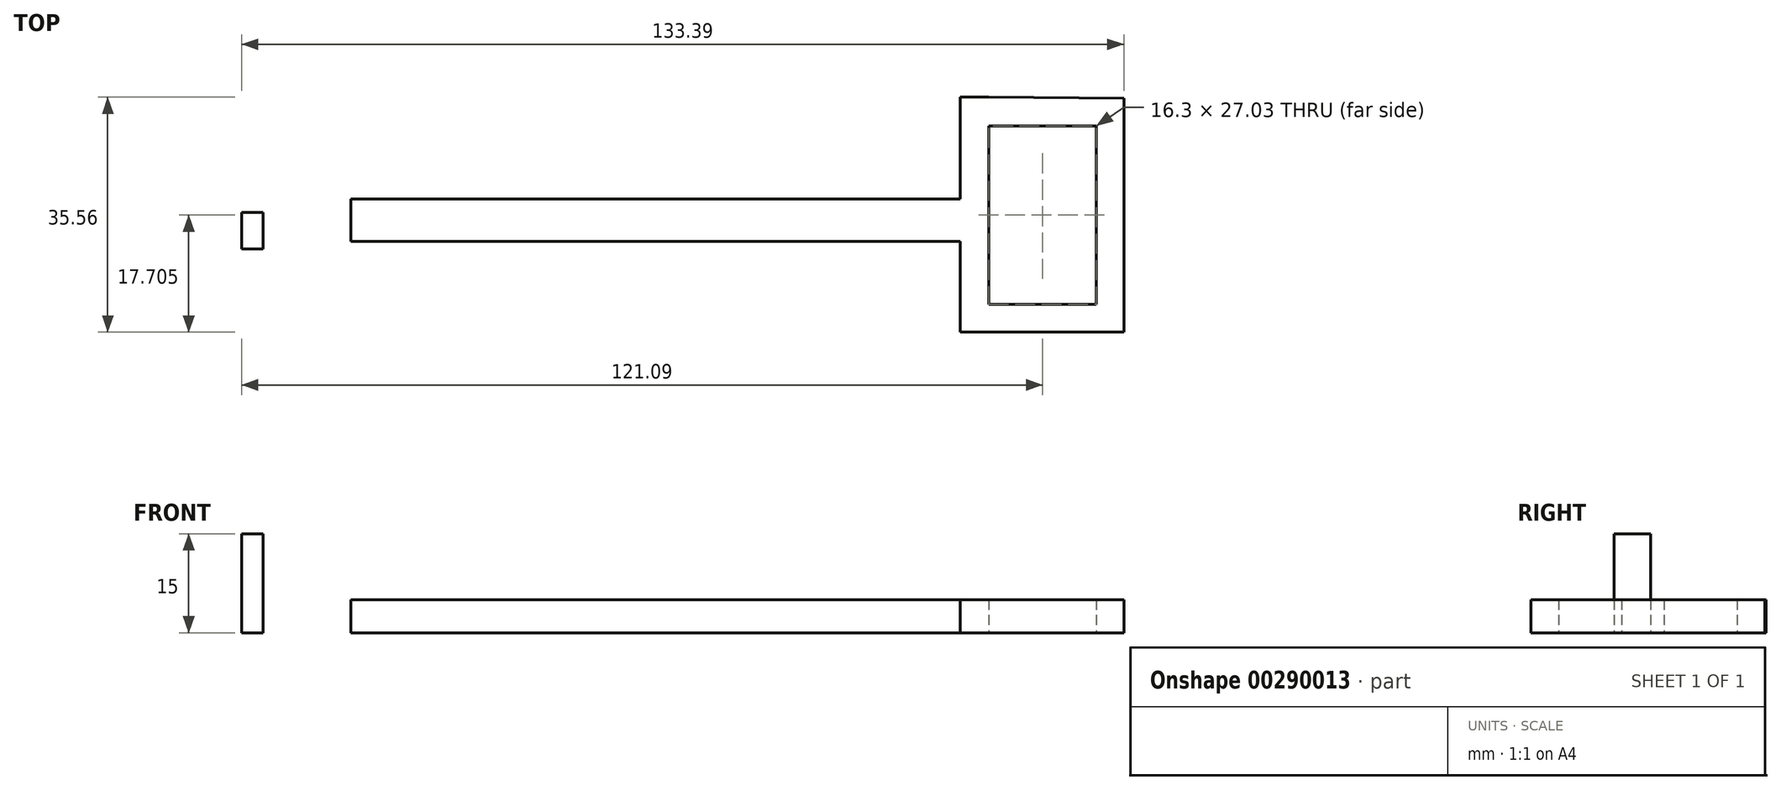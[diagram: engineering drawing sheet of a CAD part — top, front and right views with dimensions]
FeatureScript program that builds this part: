
annotation { "Feature Type Name" : "Feature", "Feature Type Description" : "" }
export const myFeature = defineFeature(function(context is Context, id is Id, definition is map)
    precondition{}
    {
        {
            var Q0;
            Q0=qCreatedBy(makeId("Top.planeOp"),FACE);
            var sketch = newSketch(context, id + "F0", { "sketchPlane" : qUnion([Q0])});
            skLineSegment(sketch, "E0.bottom", {"start": v(-7.6, -2.33) * mm, "end": v(42.14, -2.33) * mm});
            skLineSegment(sketch, "E0.top", {"start": v(-7.6, -8.73) * mm, "end": v(42.14, -8.73) * mm});
            skLineSegment(sketch, "E0.left", {"start": v(-7.6, -2.33) * mm, "end": v(-7.6, -8.73) * mm});
            skLineSegment(sketch, "E0.right", {"start": v(42.14, -2.33) * mm, "end": v(42.14, -8.73) * mm});
            skLineSegment(sketch, "E1.bottom", {"start": v(42.14, 13.07) * mm, "end": v(46.41, 13.07) * mm});
            skLineSegment(sketch, "E1.top", {"start": v(42.14, -22.49) * mm, "end": v(46.41, -22.49) * mm});
            skLineSegment(sketch, "E1.left", {"start": v(42.14, 13.07) * mm, "end": v(42.14, -22.49) * mm});
            skLineSegment(sketch, "E1.right", {"start": v(46.41, 13.07) * mm, "end": v(46.41, -22.49) * mm});
            skLineSegment(sketch, "E2.top", {"start": v(46.41, 8.73) * mm, "end": v(66.86, 8.73) * mm});
            skLineSegment(sketch, "E2.left", {"start": v(46.41, 13.07) * mm, "end": v(46.41, 8.73) * mm});
            skLineSegment(sketch, "E3.bottom", {"start": v(46.41, -22.49) * mm, "end": v(66.86, -22.49) * mm});
            skLineSegment(sketch, "E3.top", {"start": v(46.41, -18.3) * mm, "end": v(66.86, -18.3) * mm});
            skLineSegment(sketch, "E3.left", {"start": v(46.41, -22.49) * mm, "end": v(46.41, -18.3) * mm});
            skLineSegment(sketch, "E3.right", {"start": v(66.86, -22.49) * mm, "end": v(66.86, -18.3) * mm});
            skLineSegment(sketch, "E4.bottom", {"start": v(66.86, -18.3) * mm, "end": v(62.7, -18.3) * mm});
            skLineSegment(sketch, "E4.top", {"start": v(66.86, 8.73) * mm, "end": v(62.7, 8.73) * mm});
            skLineSegment(sketch, "E4.left", {"start": v(66.86, -18.3) * mm, "end": v(66.86, 8.73) * mm});
            skLineSegment(sketch, "E4.right", {"start": v(62.7, -18.3) * mm, "end": v(62.7, 8.73) * mm});
            skLineSegment(sketch, "E5", {"start": v(66.86, 12.91) * mm, "end": v(46.41, 13.07) * mm});
            skLineSegment(sketch, "E6", {"start": v(66.86, 12.91) * mm, "end": v(66.86, 8.73) * mm});
            skLineSegment(sketch, "E7", {"start": v(-7.6, -8.73) * mm, "end": v(-50.02, -8.73) * mm});
            skLineSegment(sketch, "E8", {"start": v(-50.02, -8.73) * mm, "end": v(-50.02, -2.33) * mm});
            skLineSegment(sketch, "E9", {"start": v(-50.02, -2.33) * mm, "end": v(-7.6, -2.33) * mm});
            skSolve(sketch);
        }
        {
            var Q0;
            Q0=makeQuery(id+"F0.imprint","IMPRINT",FACE,{"disambiguationData":[TD([[makeQuery(id+"F0.imprint","IMPRINT",EDGE,{"derivedFrom":sQuery(id+"F0.wireOp",EDGE,"E0.bottom")}),-1.0]])]});
            extrude(context, id + "F1", {"entities" : qUnion([Q0]), "depth" : 5 * mm});
        }
        {
            var Q0;
            Q0 = qSketchRegion(id + "F0", true);
            extrude(context, id + "F2", {"entities" : qUnion([Q0]), "operationType" : NewBodyOperationType.ADD, "depth" : 5 * mm});
        }
        {
            var Q0;
            Q0 = qSketchRegion(id + "F0", true);
            var sketch = newSketch(context, id + "F3", { "sketchPlane" : qUnion([Q0])});
            skLineSegment(sketch, "E10.KFZB.KFZB", {"start": v(-50.02, -2.33) * mm, "end": v(-7.6, -2.33) * mm, "construction": true});
            skArc(sketch, "E10.0.endCap", {"start": v(-7.6, 0.17) * mm, "mid": v(-5.1, -2.33) * mm, "end": v(-7.6, -4.83) * mm});
            skLineSegment(sketch, "E11.bottom", {"start": v(-66.53, -9.92) * mm, "end": v(-63.33, -9.92) * mm});
            skLineSegment(sketch, "E11.top", {"start": v(-66.53, -4.4) * mm, "end": v(-63.33, -4.4) * mm});
            skLineSegment(sketch, "E11.left", {"start": v(-66.53, -9.92) * mm, "end": v(-66.53, -4.4) * mm});
            skLineSegment(sketch, "E11.right", {"start": v(-63.33, -9.92) * mm, "end": v(-63.33, -4.4) * mm});
            skPoint(sketch, "E12.start.orphan", {"position": v(-70.85, -9.92) * mm});
            skSolve(sketch);
        }
        {
            var Q0;
            Q0=makeQuery(id+"F3.imprint","IMPRINT",FACE,{"disambiguationData":[TD([[makeQuery(id+"F3.imprint","IMPRINT",EDGE,{"derivedFrom":sQuery(id+"F3.wireOp",EDGE,"E11.bottom")}),1.0]])]});
            extrude(context, id + "F4", {"entities" : qUnion([Q0]), "depth" : 15 * mm});
        }
    });
